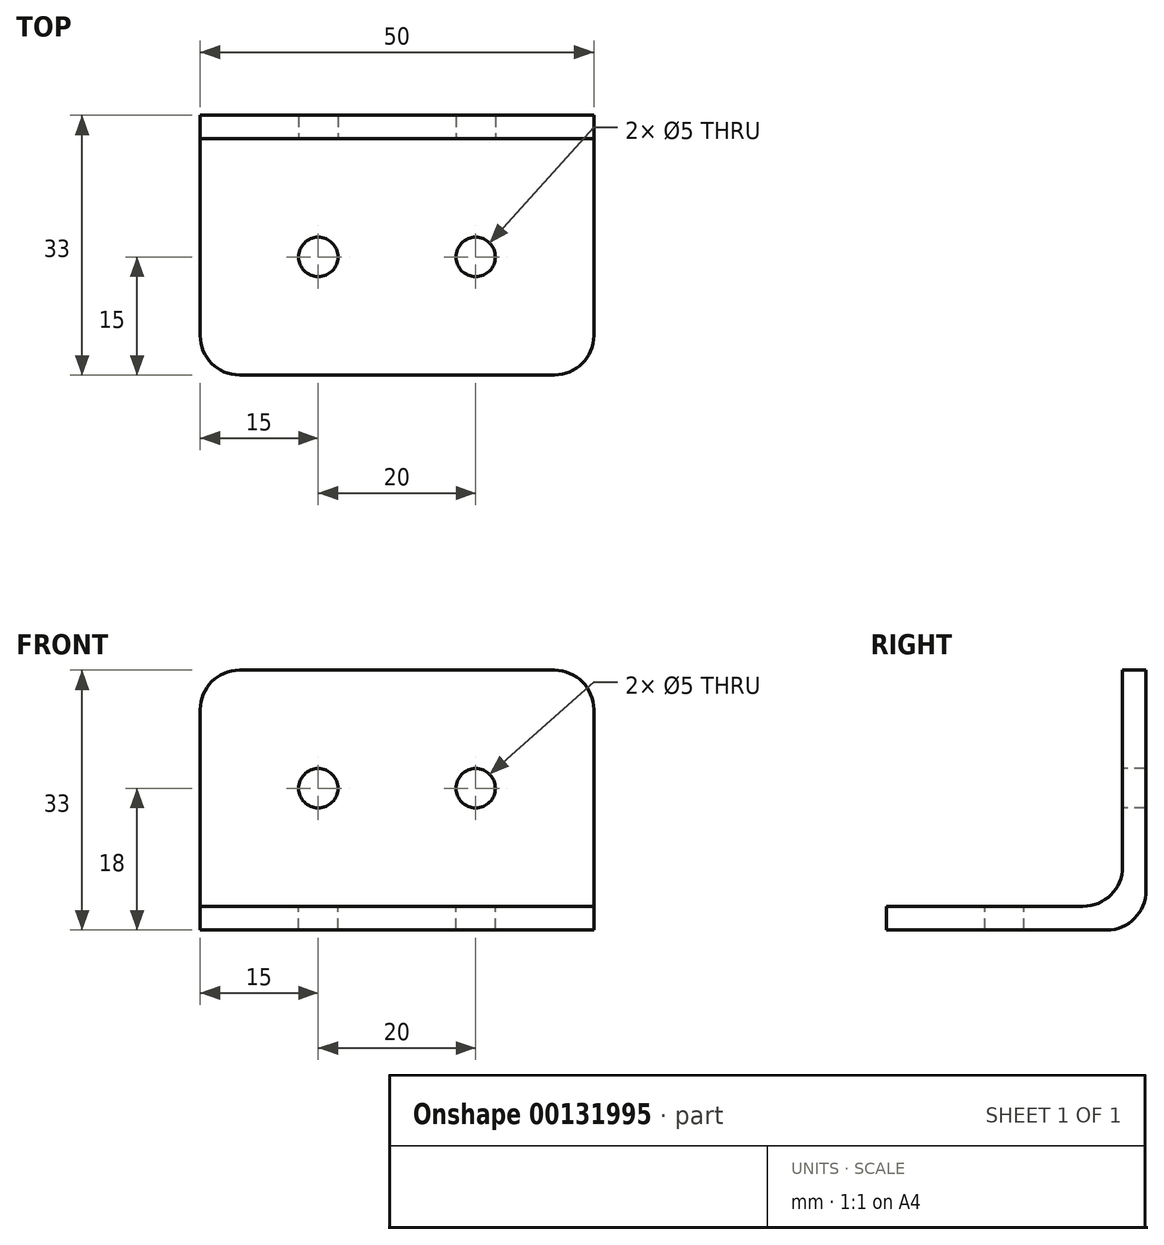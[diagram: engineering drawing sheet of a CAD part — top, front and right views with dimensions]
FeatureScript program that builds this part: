
annotation { "Feature Type Name" : "Feature", "Feature Type Description" : "" }
export const myFeature = defineFeature(function(context is Context, id is Id, definition is map)
    precondition{}
    {
        {
            var Q0;
            Q0=qCreatedBy(makeId("Top.planeOp"),FACE);
            var sketch = newSketch(context, id + "F0", { "sketchPlane" : qUnion([Q0])});
            skLineSegment(sketch, "E0.bottom", {"start": v(1210.4, -308.48) * mm, "end": v(1360.4, -308.48) * mm});
            skLineSegment(sketch, "E0.top", {"start": v(1210.4, -471.48) * mm, "end": v(1360.4, -471.48) * mm});
            skLineSegment(sketch, "E0.right", {"start": v(1360.4, -308.48) * mm, "end": v(1360.4, -471.48) * mm});
            skLineSegment(sketch, "E1", {"start": v(1210.4, -308.48) * mm, "end": v(1210.4, -471.48) * mm});
            skLineSegment(sketch, "E2.bottom", {"start": v(1125.4, -308.48) * mm, "end": v(1210.4, -308.48) * mm});
            skLineSegment(sketch, "E2.top", {"start": v(1125.4, -973.48) * mm, "end": v(1210.4, -973.48) * mm});
            skLineSegment(sketch, "E2.left", {"start": v(1125.4, -308.48) * mm, "end": v(1125.4, -973.48) * mm});
            skLineSegment(sketch, "E2.right", {"start": v(1210.4, -308.48) * mm, "end": v(1210.4, -973.48) * mm});
            skLineSegment(sketch, "E3.bottom", {"start": v(970.4, -308.48) * mm, "end": v(1125.4, -308.48) * mm});
            skLineSegment(sketch, "E3.top", {"start": v(970.4, -1054.12) * mm, "end": v(1125.4, -1054.12) * mm});
            skLineSegment(sketch, "E3.left", {"start": v(970.4, -308.48) * mm, "end": v(970.4, -1054.12) * mm});
            skLineSegment(sketch, "E3.right", {"start": v(1125.4, -308.48) * mm, "end": v(1125.4, -1054.12) * mm});
            skLineSegment(sketch, "E4.bottom", {"start": v(1210.4, -828.48) * mm, "end": v(1250.4, -828.48) * mm});
            skLineSegment(sketch, "E4.top", {"start": v(1210.4, -973.48) * mm, "end": v(1250.4, -973.48) * mm});
            skLineSegment(sketch, "E4.left", {"start": v(1210.4, -828.48) * mm, "end": v(1210.4, -973.48) * mm});
            skLineSegment(sketch, "E4.right", {"start": v(1250.4, -828.48) * mm, "end": v(1250.4, -973.48) * mm});
            skLineSegment(sketch, "E5.bottom", {"start": v(0, 0) * mm, "end": v(155, 0) * mm});
            skLineSegment(sketch, "E5.top", {"start": v(0, -665) * mm, "end": v(155, -665) * mm});
            skLineSegment(sketch, "E5.left", {"start": v(0, 0) * mm, "end": v(0, -665) * mm});
            skLineSegment(sketch, "E5.right", {"start": v(155, 0) * mm, "end": v(155, -665) * mm});
            skLineSegment(sketch, "E6.bottom", {"start": v(155, 0) * mm, "end": v(239, 0) * mm});
            skLineSegment(sketch, "E6.top", {"start": v(155, -665) * mm, "end": v(239, -665) * mm});
            skLineSegment(sketch, "E6.right", {"start": v(239, 0) * mm, "end": v(239, -665) * mm});
            skLineSegment(sketch, "E7.bottom", {"start": v(239, 0) * mm, "end": v(394, 0) * mm});
            skLineSegment(sketch, "E7.top", {"start": v(239, -163) * mm, "end": v(394, -163) * mm});
            skLineSegment(sketch, "E7.left", {"start": v(239, 0) * mm, "end": v(239, -163) * mm});
            skLineSegment(sketch, "E7.right", {"start": v(394, 0) * mm, "end": v(394, -163) * mm});
            skLineSegment(sketch, "E8.bottom", {"start": v(5, -5) * mm, "end": v(150, -5) * mm});
            skLineSegment(sketch, "E8.top", {"start": v(5, -660) * mm, "end": v(150, -660) * mm});
            skLineSegment(sketch, "E8.left", {"start": v(5, -5) * mm, "end": v(5, -660) * mm});
            skLineSegment(sketch, "E8.right", {"start": v(150, -5) * mm, "end": v(150, -660) * mm});
            skLineSegment(sketch, "E9.bottom", {"start": v(168, -5) * mm, "end": v(226, -5) * mm});
            skLineSegment(sketch, "E9.top", {"start": v(168, -660) * mm, "end": v(226, -660) * mm});
            skLineSegment(sketch, "E9.left", {"start": v(168, -5) * mm, "end": v(168, -660) * mm});
            skLineSegment(sketch, "E9.right", {"start": v(226, -5) * mm, "end": v(226, -660) * mm});
            skLineSegment(sketch, "E10.bottom", {"start": v(244, -5) * mm, "end": v(389, -5) * mm});
            skLineSegment(sketch, "E10.top", {"start": v(244, -158) * mm, "end": v(389, -158) * mm});
            skLineSegment(sketch, "E10.left", {"start": v(244, -5) * mm, "end": v(244, -158) * mm});
            skLineSegment(sketch, "E10.right", {"start": v(389, -5) * mm, "end": v(389, -158) * mm});
            skLineSegment(sketch, "E11", {"start": v(5, -5) * mm, "end": v(5, 0) * mm});
            skLineSegment(sketch, "E12", {"start": v(5, -660) * mm, "end": v(5, -665) * mm});
            skLineSegment(sketch, "E13", {"start": v(150, -660) * mm, "end": v(150, -665) * mm});
            skLineSegment(sketch, "E14", {"start": v(150, -5) * mm, "end": v(155, -5) * mm});
            skPoint(sketch, "E15.end.orphan", {"position": v(0, -660) * mm});
            skSolve(sketch);
        }
        {
            var Q0;
            Q0=makeQuery(id+"F0.imprint","IMPRINT",FACE,{"disambiguationData":[TD([[makeQuery(id+"F0.imprint","IMPRINT",EDGE,{"derivedFrom":sQuery(id+"F0.wireOp",EDGE,"E5.bottom")}),-1.0]])]});
            var Q1;
            {var subQ0=sQuery(id+"F0.wireOp",EDGE,"E5.left");Q1=makeQuery(id+"F0.imprint","IMPRINT",FACE,{"disambiguationData":[TD([[makeQuery(id+"F0.imprint","IMPRINT",EDGE,{"derivedFrom":subQ0}),1.0]])]});}
            var Q2;
            Q2=makeQuery(id+"F0.imprint","IMPRINT",FACE,{"disambiguationData":[TD([[makeQuery(id+"F0.imprint","IMPRINT",EDGE,{"derivedFrom":sQuery(id+"F0.wireOp",EDGE,"E8.right")}),1.0]])]});
            var Q3;
            Q3=makeQuery(id+"F0.imprint","IMPRINT",FACE,{"disambiguationData":[TD([[makeQuery(id+"F0.imprint","IMPRINT",EDGE,{"derivedFrom":sQuery(id+"F0.wireOp",EDGE,"E8.top")}),-1.0]])]});
            extrude(context, id + "F1", {"entities" : qUnion([Q0, Q1, Q2, Q3]), "oppositeDirection" : true, "depth" : 360 * mm});
        }
        {
            var Q0;
            Q0=makeQuery(id+"F0.imprint","IMPRINT",FACE,{"disambiguationData":[TD([[makeQuery(id+"F0.imprint","IMPRINT",EDGE,{"derivedFrom":sQuery(id+"F0.wireOp",EDGE,"E6.bottom")}),-1.0]])]});
            extrude(context, id + "F2", {"entities" : qUnion([Q0]), "oppositeDirection" : true, "depth" : 360 * mm});
        }
        {
            var Q0;
            Q0=makeQuery(id+"F0.imprint","IMPRINT",FACE,{"disambiguationData":[TD([[makeQuery(id+"F0.imprint","IMPRINT",EDGE,{"derivedFrom":sQuery(id+"F0.wireOp",EDGE,"E7.bottom")}),-1.0]])]});
            extrude(context, id + "F3", {"entities" : qUnion([Q0]), "oppositeDirection" : true, "depth" : 360 * mm});
        }
        {
            var Q0;
            Q0=makeQuery(id+"F1.opExtrude","SWEPT_FACE",FACE,{"disambiguationData":[OSD([sQuery(id+"F0.wireOp",EDGE,"E5.bottom")])]});
            var sketch = newSketch(context, id + "F4", { "sketchPlane" : qUnion([Q0])});
            skLineSegment(sketch, "E16", {"start": v(0, -360) * mm, "end": v(0, -330) * mm});
            skLineSegment(sketch, "E17", {"start": v(0, -330) * mm, "end": v(1, -330) * mm});
            skLineSegment(sketch, "E18", {"start": v(1, -330) * mm, "end": v(1, -359) * mm});
            skLineSegment(sketch, "E19", {"start": v(1, -359) * mm, "end": v(30, -359) * mm});
            skLineSegment(sketch, "E20", {"start": v(30, -359) * mm, "end": v(30, -360) * mm});
            skLineSegment(sketch, "E21", {"start": v(30, -360) * mm, "end": v(0, -360) * mm});
            skSolve(sketch);
        }
        {
            var Q0;
            Q0=qSketchRegion(id+"F4",true);
            extrude(context, id + "F5", {"entities" : qUnion([Q0]), "oppositeDirection" : true, "depth" : 665 * mm});
        }
        {
            var Q0;
            Q0=makeQuery(id+"F3.opExtrude","SWEPT_FACE",FACE,{"disambiguationData":[OSD([sQuery(id+"F0.wireOp",EDGE,"E7.right")])]});
            var sketch = newSketch(context, id + "F6", { "sketchPlane" : qUnion([Q0])});
            skLineSegment(sketch, "E22", {"start": v(0, -360) * mm, "end": v(0, -330) * mm});
            skLineSegment(sketch, "E23", {"start": v(0, -330) * mm, "end": v(1, -330) * mm});
            skLineSegment(sketch, "E24", {"start": v(1, -330) * mm, "end": v(1, -359) * mm});
            skLineSegment(sketch, "E25", {"start": v(1, -359) * mm, "end": v(30, -359) * mm});
            skLineSegment(sketch, "E26", {"start": v(30, -359) * mm, "end": v(30, -360) * mm});
            skLineSegment(sketch, "E27", {"start": v(30, -360) * mm, "end": v(0, -360) * mm});
            skSolve(sketch);
        }
        {
            var Q0;
            Q0=qSketchRegion(id+"F6",true);
            extrude(context, id + "F7", {"entities" : qUnion([Q0]), "oppositeDirection" : true, "depth" : 394 * mm});
        }
        {
            var Q0;
            Q0=makeQuery(id+"F3.opExtrude","SWEPT_FACE",FACE,{"disambiguationData":[OSD([sQuery(id+"F0.wireOp",EDGE,"E7.right")])]});
            var sketch = newSketch(context, id + "F8", { "sketchPlane" : qUnion([Q0])});
            skLineSegment(sketch, "E28", {"start": v(-163, -360) * mm, "end": v(-163, -330) * mm});
            skLineSegment(sketch, "E29", {"start": v(-163, -330) * mm, "end": v(-164, -330) * mm});
            skLineSegment(sketch, "E30", {"start": v(-164, -330) * mm, "end": v(-164, -359) * mm});
            skLineSegment(sketch, "E31", {"start": v(-164, -359) * mm, "end": v(-193, -359) * mm});
            skLineSegment(sketch, "E32", {"start": v(-193, -359) * mm, "end": v(-193, -360) * mm});
            skLineSegment(sketch, "E33", {"start": v(-193, -360) * mm, "end": v(-163, -360) * mm});
            skSolve(sketch);
        }
        {
            var Q0;
            Q0=qSketchRegion(id+"F8",true);
            extrude(context, id + "F9", {"entities" : qUnion([Q0]), "oppositeDirection" : true, "depth" : 125 * mm});
        }
        {
            var Q0;
            Q0=makeQuery(id+"F2.opExtrude","SWEPT_FACE",FACE,{"disambiguationData":[OSD([sQuery(id+"F0.wireOp",EDGE,"E6.right"),sQuery(id+"F0.wireOp",EDGE,"E7.left")])]});
            var sketch = newSketch(context, id + "F10", { "sketchPlane" : qUnion([Q0])});
            skLineSegment(sketch, "E34", {"start": v(-665, -360) * mm, "end": v(-665, -327) * mm});
            skLineSegment(sketch, "E35", {"start": v(-665, -327) * mm, "end": v(-668, -327) * mm});
            skLineSegment(sketch, "E36", {"start": v(-668, -327) * mm, "end": v(-668, -357) * mm});
            skLineSegment(sketch, "E37", {"start": v(-668, -357) * mm, "end": v(-698, -357) * mm});
            skLineSegment(sketch, "E38", {"start": v(-698, -357) * mm, "end": v(-698, -360) * mm});
            skLineSegment(sketch, "E39", {"start": v(-698, -360) * mm, "end": v(-665, -360) * mm});
            skSolve(sketch);
        }
        {
            var Q0;
            Q0=qSketchRegion(id+"F10",true);
            extrude(context, id + "F11", {"entities" : qUnion([Q0]), "oppositeDirection" : true, "depth" : 50 * mm});
        }
        {
            var Q0;
            Q0=makeQuery(id+"F11.opExtrude","SWEPT_EDGE",EDGE,{"disambiguationData":[OSD([sQuery(id+"F10.wireOp",EDGE,"E36"),sQuery(id+"F10.wireOp",EDGE,"E37")])]});
            var Q1;
            Q1=makeQuery(id+"F11.opExtrude","CAP_EDGE",EDGE,{"disambiguationData":[OSD([sQuery(id+"F10.wireOp",EDGE,"E35")])],"isStart":false});
            var Q2;
            Q2=makeQuery(id+"F11.opExtrude","CAP_EDGE",EDGE,{"disambiguationData":[OSD([sQuery(id+"F10.wireOp",EDGE,"E35")])],"isStart":true});
            var Q3;
            Q3=makeQuery(id+"F11.opExtrude","CAP_EDGE",EDGE,{"disambiguationData":[OSD([sQuery(id+"F10.wireOp",EDGE,"E38")])],"isStart":true});
            var Q4;
            Q4=makeQuery(id+"F11.opExtrude","CAP_EDGE",EDGE,{"disambiguationData":[OSD([sQuery(id+"F10.wireOp",EDGE,"E38")])],"isStart":false});
            var Q5;
            Q5=makeQuery(id+"F11.opExtrude","SWEPT_EDGE",EDGE,{"disambiguationData":[OSD([sQuery(id+"F0.wireOp",EDGE,"E6.right"),sQuery(id+"F0.wireOp",EDGE,"E7.left"),sQuery(id+"F10.wireOp",EDGE,"E34"),sQuery(id+"F10.wireOp",EDGE,"E39")])]});
            fillet(context, id + "F12", {"entities" : qUnion([Q0, Q1, Q2, Q3, Q4, Q5]), "radius" : 5 * mm, "tangentPropagation" : true, "allowEdgeOverflow" : false});
        }
        {
            var Q0;
            Q0=makeQuery(id+"F11.opExtrude","SWEPT_FACE",FACE,{"disambiguationData":[OSD([sQuery(id+"F10.wireOp",EDGE,"E37")])]});
            var sketch = newSketch(context, id + "F13", { "sketchPlane" : qUnion([Q0])});
            skCircle(sketch, "E40", {"center": v(204, -683) * mm, "radius": 2.5 * mm});
            skCircle(sketch, "E41", {"center": v(224, -683) * mm, "radius": 2.5 * mm});
            skSolve(sketch);
        }
        {
            var Q0;
            Q0=makeQuery(id+"F11.opExtrude","SWEPT_FACE",FACE,{"disambiguationData":[OSD([sQuery(id+"F10.wireOp",EDGE,"E36")])]});
            var sketch = newSketch(context, id + "F14", { "sketchPlane" : qUnion([Q0])});
            skCircle(sketch, "E42", {"center": v(204, -342) * mm, "radius": 2.5 * mm});
            skCircle(sketch, "E43", {"center": v(224, -342) * mm, "radius": 2.5 * mm});
            skSolve(sketch);
        }
        {
            var Q0;
            Q0=qSketchRegion(id+"F14",true);
            extrude(context, id + "F15", {"entities" : qUnion([Q0]), "operationType" : NewBodyOperationType.REMOVE, "oppositeDirection" : true, "depth" : 10 * mm});
        }
        {
            var Q0;
            Q0=qSketchRegion(id+"F13",true);
            extrude(context, id + "F16", {"entities" : qUnion([Q0]), "operationType" : NewBodyOperationType.REMOVE, "oppositeDirection" : true, "depth" : 10 * mm});
        }
        {
            var Q0;
            Q0=makeQuery(id+"F2.opExtrude","SWEPT_FACE",FACE,{"disambiguationData":[OSD([sQuery(id+"F0.wireOp",EDGE,"E6.top")])]});
            var sketch = newSketch(context, id + "F17", { "sketchPlane" : qUnion([Q0])});
            skLineSegment(sketch, "E44", {"start": v(239, -330) * mm, "end": v(239, -360) * mm});
            skLineSegment(sketch, "E45", {"start": v(239, -360) * mm, "end": v(269, -360) * mm});
            skLineSegment(sketch, "E46", {"start": v(269, -360) * mm, "end": v(269, -357) * mm});
            skLineSegment(sketch, "E47", {"start": v(269, -357) * mm, "end": v(242, -357) * mm});
            skLineSegment(sketch, "E48", {"start": v(242, -357) * mm, "end": v(242, -330) * mm});
            skLineSegment(sketch, "E49", {"start": v(242, -330) * mm, "end": v(239, -330) * mm});
            skSolve(sketch);
        }
        {
            var Q0;
            Q0=qSketchRegion(id+"F17",true);
            extrude(context, id + "F18", {"entities" : qUnion([Q0]), "oppositeDirection" : true, "depth" : 502 * mm});
        }
        {
            var Q0;
            Q0=makeQuery(id+"F1.opExtrude","SWEPT_BODY",BODY,{"disambiguationData":[OSD([sQuery(id+"F0.wireOp",EDGE,"E5.bottom"),sQuery(id+"F0.wireOp",EDGE,"E5.top"),sQuery(id+"F0.wireOp",EDGE,"E5.left"),sQuery(id+"F0.wireOp",EDGE,"E5.right"),sQuery(id+"F0.wireOp",EDGE,"E8.bottom"),sQuery(id+"F0.wireOp",EDGE,"E8.top"),sQuery(id+"F0.wireOp",EDGE,"E8.left"),sQuery(id+"F0.wireOp",EDGE,"E8.right")])]});
            var Q1;
            Q1=makeQuery(id+"F2.opExtrude","SWEPT_BODY",BODY,{"disambiguationData":[OSD([sQuery(id+"F0.wireOp",EDGE,"E6.bottom"),sQuery(id+"F0.wireOp",EDGE,"E6.top"),sQuery(id+"F0.wireOp",EDGE,"E5.right"),sQuery(id+"F0.wireOp",EDGE,"E6.right"),sQuery(id+"F0.wireOp",EDGE,"E7.left"),sQuery(id+"F0.wireOp",EDGE,"E9.bottom"),sQuery(id+"F0.wireOp",EDGE,"E9.top"),sQuery(id+"F0.wireOp",EDGE,"E9.left"),sQuery(id+"F0.wireOp",EDGE,"E9.right")])]});
            var Q2;
            Q2=makeQuery(id+"F3.opExtrude","SWEPT_BODY",BODY,{"disambiguationData":[OSD([sQuery(id+"F0.wireOp",EDGE,"E7.bottom"),sQuery(id+"F0.wireOp",EDGE,"E7.top"),sQuery(id+"F0.wireOp",EDGE,"E7.left"),sQuery(id+"F0.wireOp",EDGE,"E7.right"),sQuery(id+"F0.wireOp",EDGE,"E10.bottom"),sQuery(id+"F0.wireOp",EDGE,"E10.top"),sQuery(id+"F0.wireOp",EDGE,"E10.left"),sQuery(id+"F0.wireOp",EDGE,"E10.right")])]});
            var Q3;
            Q3=makeQuery(id+"F5.opExtrude","SWEPT_BODY",BODY,{"disambiguationData":[OSD([sQuery(id+"F4.wireOp",EDGE,"E16"),sQuery(id+"F4.wireOp",EDGE,"E17"),sQuery(id+"F4.wireOp",EDGE,"E18"),sQuery(id+"F4.wireOp",EDGE,"E19"),sQuery(id+"F4.wireOp",EDGE,"E20"),sQuery(id+"F4.wireOp",EDGE,"E21")])]});
            var Q4;
            Q4=makeQuery(id+"F7.opExtrude","SWEPT_BODY",BODY,{"disambiguationData":[OSD([sQuery(id+"F6.wireOp",EDGE,"E22"),sQuery(id+"F6.wireOp",EDGE,"E23"),sQuery(id+"F6.wireOp",EDGE,"E24"),sQuery(id+"F6.wireOp",EDGE,"E25"),sQuery(id+"F6.wireOp",EDGE,"E26"),sQuery(id+"F6.wireOp",EDGE,"E27")])]});
            var Q5;
            Q5=makeQuery(id+"F9.opExtrude","SWEPT_BODY",BODY,{"disambiguationData":[OSD([sQuery(id+"F8.wireOp",EDGE,"E28"),sQuery(id+"F8.wireOp",EDGE,"E29"),sQuery(id+"F8.wireOp",EDGE,"E30"),sQuery(id+"F8.wireOp",EDGE,"E31"),sQuery(id+"F8.wireOp",EDGE,"E32"),sQuery(id+"F8.wireOp",EDGE,"E33")])]});
            deleteBodies(context, id + "F19", {"entities" : qUnion([Q0, Q1, Q2, Q3, Q4, Q5])});
        }
        {
            var Q0;
            Q0=makeQuery(id+"F18.opExtrude","SWEPT_BODY",BODY,{"disambiguationData":[OSD([sQuery(id+"F17.wireOp",EDGE,"E44"),sQuery(id+"F17.wireOp",EDGE,"E45"),sQuery(id+"F17.wireOp",EDGE,"E46"),sQuery(id+"F17.wireOp",EDGE,"E47"),sQuery(id+"F17.wireOp",EDGE,"E48"),sQuery(id+"F17.wireOp",EDGE,"E49")])]});
            var Q1;
            Q1=makeQuery(id+"FoKapciyiGmig6i_7.opExtrude","SWEPT_BODY",BODY,{"disambiguationData":[OSD([sQuery(id+"Fubqy5WX5NT4bja_7.wireOp",EDGE,"QP4V10lX-q36o-5SO8-uj40-fgyMPsIonrLo.bottom"),sQuery(id+"Fubqy5WX5NT4bja_7.wireOp",EDGE,"QP4V10lX-q36o-5SO8-uj40-fgyMPsIonrLo.top"),sQuery(id+"Fubqy5WX5NT4bja_7.wireOp",EDGE,"QP4V10lX-q36o-5SO8-uj40-fgyMPsIonrLo.left"),sQuery(id+"Fubqy5WX5NT4bja_7.wireOp",EDGE,"QP4V10lX-q36o-5SO8-uj40-fgyMPsIonrLo.right")])]});
            var Q2;
            Q2=makeQuery(id+"F9W7Hv5DZ8duFvO_8.opExtrude","SWEPT_BODY",BODY,{"disambiguationData":[OSD([sQuery(id+"FlWkDR7D6poDUkY_8.wireOp",EDGE,"OMuCjIfV-DdZw-qft9-ulAN-3gdCwVp6CZH7.bottom"),sQuery(id+"FlWkDR7D6poDUkY_8.wireOp",EDGE,"OMuCjIfV-DdZw-qft9-ulAN-3gdCwVp6CZH7.top"),sQuery(id+"FlWkDR7D6poDUkY_8.wireOp",EDGE,"OMuCjIfV-DdZw-qft9-ulAN-3gdCwVp6CZH7.left"),sQuery(id+"FlWkDR7D6poDUkY_8.wireOp",EDGE,"OMuCjIfV-DdZw-qft9-ulAN-3gdCwVp6CZH7.right")])]});
            var Q3;
            Q3=makeQuery(id+"FinnnRAn1l1iBQT_9.opExtrude","SWEPT_BODY",BODY,{"disambiguationData":[OSD([sQuery(id+"F0OHpSnM6vH6uVN_9.wireOp",EDGE,"AdY77VuX-DhKt-YVth-ewQ3-so38mTrboc7k.bottom"),sQuery(id+"F0OHpSnM6vH6uVN_9.wireOp",EDGE,"AdY77VuX-DhKt-YVth-ewQ3-so38mTrboc7k.top"),sQuery(id+"F0OHpSnM6vH6uVN_9.wireOp",EDGE,"AdY77VuX-DhKt-YVth-ewQ3-so38mTrboc7k.left"),sQuery(id+"F0OHpSnM6vH6uVN_9.wireOp",EDGE,"AdY77VuX-DhKt-YVth-ewQ3-so38mTrboc7k.right")])]});
            deleteBodies(context, id + "F20", {"entities" : qUnion([Q0, Q1, Q2, Q3])});
        }
    });
